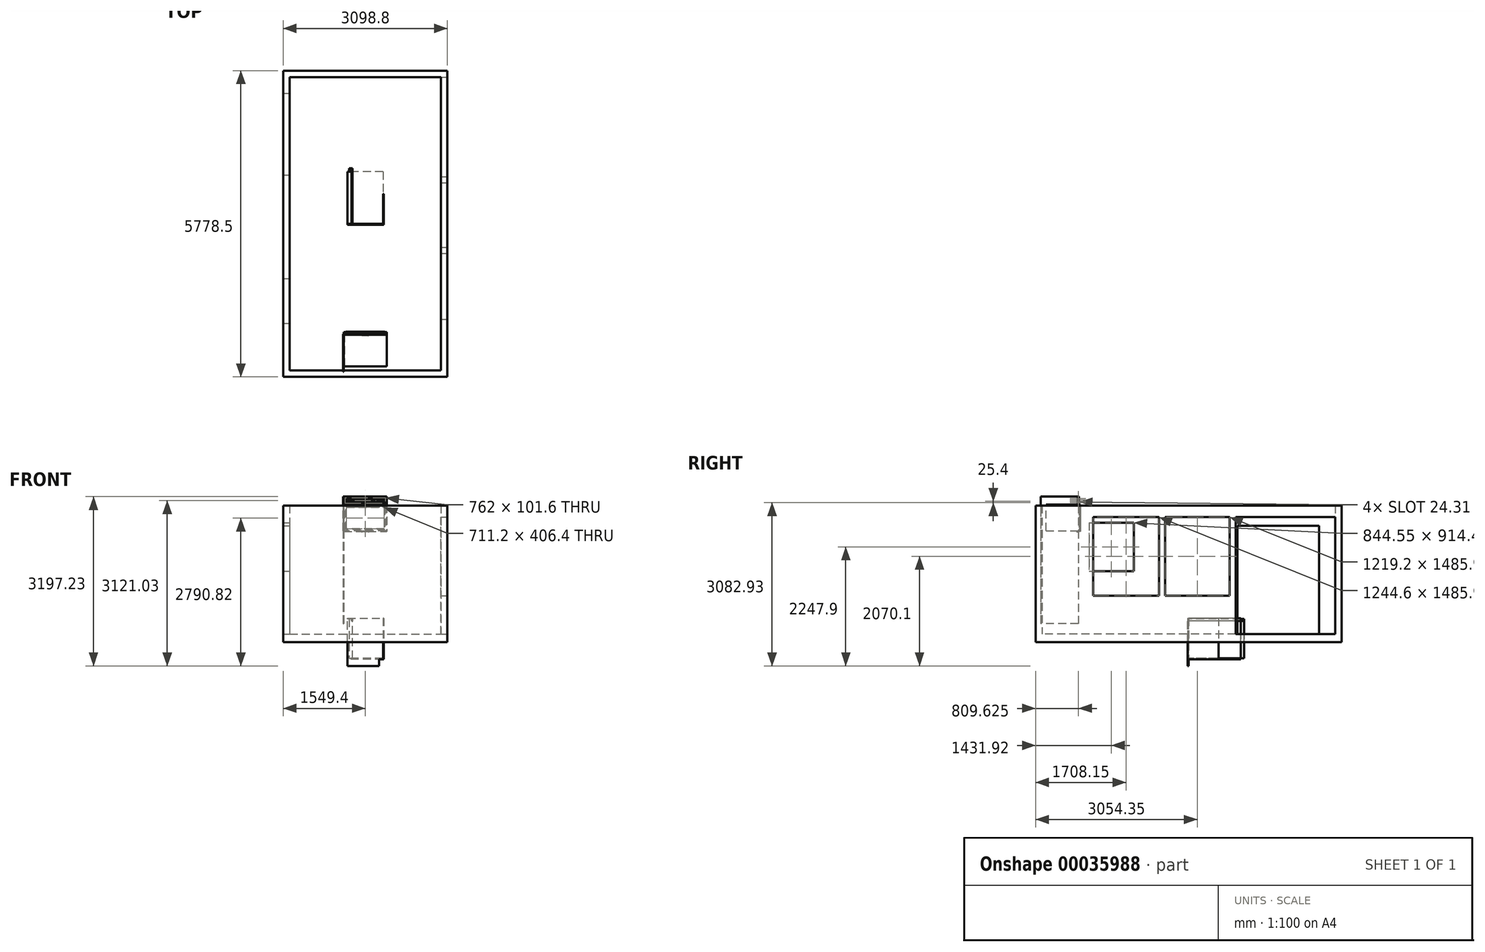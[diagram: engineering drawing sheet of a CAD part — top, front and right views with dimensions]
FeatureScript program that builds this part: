
annotation { "Feature Type Name" : "Feature", "Feature Type Description" : "" }
export const myFeature = defineFeature(function(context is Context, id is Id, definition is map)
    precondition{}
    {
        {
            var Q0;
            Q0=qCreatedBy(makeId("Top.planeOp"),FACE);
            var sketch = newSketch(context, id + "F0", { "sketchPlane" : qUnion([Q0])});
            skLineSegment(sketch, "E0.bottom", {"start": v(-1549.4, 2889.25) * mm, "end": v(1549.4, 2889.25) * mm});
            skLineSegment(sketch, "E0.top", {"start": v(-1549.4, -2889.25) * mm, "end": v(1549.4, -2889.25) * mm});
            skLineSegment(sketch, "E0.left", {"start": v(-1549.4, 2889.25) * mm, "end": v(-1549.4, -2889.25) * mm});
            skLineSegment(sketch, "E0.right", {"start": v(1549.4, 2889.25) * mm, "end": v(1549.4, -2889.25) * mm});
            skLineSegment(sketch, "E1", {"start": v(1549.4, 2889.25) * mm, "end": v(-1549.4, -2889.25) * mm, "construction": true});
            skSolve(sketch);
        }
        {
            var Q0;
            Q0 = qSketchRegion(id + "F0", true);
            extrude(context, id + "F1", {"entities" : qUnion([Q0]), "depth" : 152.4 * mm});
        }
        {
            var Q0;
            Q0=makeQuery(id+"F1.opExtrude","CAP_FACE",FACE,{"disambiguationData":[OSD([sQuery(id+"F0.wireOp",EDGE,"E0.bottom"),sQuery(id+"F0.wireOp",EDGE,"E0.top"),sQuery(id+"F0.wireOp",EDGE,"E0.left"),sQuery(id+"F0.wireOp",EDGE,"E0.right")])],"isStart":false});
            var sketch = newSketch(context, id + "F2", { "sketchPlane" : qUnion([Q0])});
            skLineSegment(sketch, "E2.0", {"start": v(-1549.4, 2889.25) * mm, "end": v(-1549.4, -2889.25) * mm});
            skLineSegment(sketch, "E3.0", {"start": v(-1549.4, -2889.25) * mm, "end": v(1549.4, -2889.25) * mm});
            skLineSegment(sketch, "E4.0", {"start": v(1549.4, 2889.25) * mm, "end": v(1549.4, -2889.25) * mm});
            skLineSegment(sketch, "E5.0", {"start": v(-1549.4, 2889.25) * mm, "end": v(1549.4, 2889.25) * mm});
            skLineSegment(sketch, "E6.0", {"start": v(-1428.75, 2768.6) * mm, "end": v(-1428.75, -2768.6) * mm});
            skLineSegment(sketch, "E6.1", {"start": v(-1428.75, 2768.6) * mm, "end": v(1428.75, 2768.6) * mm});
            skLineSegment(sketch, "E6.2", {"start": v(1428.75, 2768.6) * mm, "end": v(1428.75, -2768.6) * mm});
            skLineSegment(sketch, "E6.3", {"start": v(-1428.75, -2768.6) * mm, "end": v(1428.75, -2768.6) * mm});
            skSolve(sketch);
        }
        {
            var Q0;
            Q0=makeQuery(id+"F2.imprint","IMPRINT",FACE,{"disambiguationData":[TD([[makeQuery(id+"F2.imprint","IMPRINT",EDGE,{"derivedFrom":sQuery(id+"F2.wireOp",EDGE,"E2.0")}),1.0]])]});
            extrude(context, id + "F3", {"entities" : qUnion([Q0]), "operationType" : NewBodyOperationType.ADD, "depth" : 2425.7 * mm});
        }
        {
            var Q0;
            Q0=makeQuery(id+"F3.boolean.opBoolean","MERGE",FACE,{"derivedFrom":[makeQuery(id+"F1.opExtrude","SWEPT_FACE",FACE,{"disambiguationData":[OSD([sQuery(id+"F0.wireOp",EDGE,"E0.right")])]}),makeQuery(id+"F3.opExtrude","SWEPT_FACE",FACE,{"disambiguationData":[OSD([sQuery(id+"F2.wireOp",EDGE,"E4.0")])]})]});
            var sketch = newSketch(context, id + "F4", { "sketchPlane" : qUnion([Q0])});
            skLineSegment(sketch, "E7.0", {"start": v(2768.6, 2578.1) * mm, "end": v(2768.6, 152.4) * mm, "construction": true});
            skLineSegment(sketch, "E8.0", {"start": v(2768.6, 152.4) * mm, "end": v(-2768.6, 152.4) * mm, "construction": true});
            skLineSegment(sketch, "E9.0", {"start": v(2768.6, 2362.2) * mm, "end": v(-2768.6, 2362.2) * mm, "construction": true});
            skLineSegment(sketch, "E10.bottom", {"start": v(889, 2362.2) * mm, "end": v(2768.6, 2362.2) * mm});
            skLineSegment(sketch, "E10.top", {"start": v(889, 152.4) * mm, "end": v(2768.6, 152.4) * mm});
            skLineSegment(sketch, "E10.left", {"start": v(889, 2362.2) * mm, "end": v(889, 152.4) * mm});
            skLineSegment(sketch, "E10.right", {"start": v(2768.6, 2362.2) * mm, "end": v(2768.6, 152.4) * mm});
            skSolve(sketch);
        }
        {
            var Q0;
            Q0=makeQuery(id+"F4.imprint","IMPRINT",FACE,{"disambiguationData":[TD([[makeQuery(id+"F4.imprint","IMPRINT",EDGE,{"derivedFrom":sQuery(id+"F4.wireOp",EDGE,"E10.bottom")}),-1.0]])]});
            var Q1;
            Q1=makeQuery(id+"F3.opExtrude","SWEPT_FACE",FACE,{"disambiguationData":[OSD([sQuery(id+"F2.wireOp",EDGE,"E6.2")])]});
            extrude(context, id + "F5", {"entities" : qUnion([Q0]), "operationType" : NewBodyOperationType.REMOVE, "endBound" : BoundingType.UP_TO_SURFACE, "oppositeDirection" : true, "endBoundEntityFace" : qUnion([Q1]), "depth" : 25.4 * mm});
        }
        {
            var Q0;
            Q0=makeQuery(id+"F3.boolean.opBoolean","MERGE",FACE,{"derivedFrom":[makeQuery(id+"F1.opExtrude","SWEPT_FACE",FACE,{"disambiguationData":[OSD([sQuery(id+"F0.wireOp",EDGE,"E0.right")])]}),makeQuery(id+"F3.opExtrude","SWEPT_FACE",FACE,{"disambiguationData":[OSD([sQuery(id+"F2.wireOp",EDGE,"E4.0")])]})]});
            var sketch = newSketch(context, id + "F6", { "sketchPlane" : qUnion([Q0])});
            skLineSegment(sketch, "E11.bottom", {"start": v(-1803.4, 2362.2) * mm, "end": v(-558.8, 2362.2) * mm});
            skLineSegment(sketch, "E11.top", {"start": v(-1803.4, 876.3) * mm, "end": v(-558.8, 876.3) * mm});
            skLineSegment(sketch, "E11.left", {"start": v(-1803.4, 2362.2) * mm, "end": v(-1803.4, 876.3) * mm});
            skLineSegment(sketch, "E11.right", {"start": v(-558.8, 2362.2) * mm, "end": v(-558.8, 876.3) * mm});
            skLineSegment(sketch, "E12.bottom", {"start": v(-444.5, 2362.2) * mm, "end": v(774.7, 2362.2) * mm});
            skLineSegment(sketch, "E12.top", {"start": v(-444.5, 876.3) * mm, "end": v(774.7, 876.3) * mm});
            skLineSegment(sketch, "E12.left", {"start": v(-444.5, 2362.2) * mm, "end": v(-444.5, 876.3) * mm});
            skLineSegment(sketch, "E12.right", {"start": v(774.7, 2362.2) * mm, "end": v(774.7, 876.3) * mm});
            skLineSegment(sketch, "E13.0", {"start": v(-2768.6, 2578.1) * mm, "end": v(-2768.6, 152.4) * mm, "construction": true});
            skSolve(sketch);
        }
        {
            var Q0;
            Q0=makeQuery(id+"F6.imprint","IMPRINT",FACE,{"disambiguationData":[TD([[makeQuery(id+"F6.imprint","IMPRINT",EDGE,{"derivedFrom":sQuery(id+"F6.wireOp",EDGE,"E12.bottom")}),-1.0]])]});
            var Q1;
            Q1=makeQuery(id+"F6.imprint","IMPRINT",FACE,{"disambiguationData":[TD([[makeQuery(id+"F6.imprint","IMPRINT",EDGE,{"derivedFrom":sQuery(id+"F6.wireOp",EDGE,"E11.bottom")}),-1.0]])]});
            var Q2;
            Q2=makeQuery(id+"F3.opExtrude","SWEPT_FACE",FACE,{"disambiguationData":[OSD([sQuery(id+"F2.wireOp",EDGE,"E6.2")])]});
            extrude(context, id + "F7", {"entities" : qUnion([Q0, Q1]), "operationType" : NewBodyOperationType.REMOVE, "endBound" : BoundingType.UP_TO_SURFACE, "oppositeDirection" : true, "endBoundEntityFace" : qUnion([Q2]), "depth" : 25.4 * mm});
        }
        {
            var Q0;
            Q0=makeQuery(id+"F3.opExtrude","SWEPT_FACE",FACE,{"disambiguationData":[OSD([sQuery(id+"F2.wireOp",EDGE,"E6.0")])]});
            var sketch = newSketch(context, id + "F8", { "sketchPlane" : qUnion([Q0])});
            skLineSegment(sketch, "E14.bottom", {"start": v(-1879.6, 2254.25) * mm, "end": v(-1035.05, 2254.25) * mm});
            skLineSegment(sketch, "E14.top", {"start": v(-1879.6, 1339.85) * mm, "end": v(-1035.05, 1339.85) * mm});
            skLineSegment(sketch, "E14.left", {"start": v(-1879.6, 2254.25) * mm, "end": v(-1879.6, 1339.85) * mm});
            skLineSegment(sketch, "E14.right", {"start": v(-1035.05, 2254.25) * mm, "end": v(-1035.05, 1339.85) * mm});
            skSolve(sketch);
        }
        {
            var Q0;
            Q0=makeQuery(id+"F8.imprint","IMPRINT",FACE,{"disambiguationData":[TD([[makeQuery(id+"F8.imprint","IMPRINT",EDGE,{"derivedFrom":sQuery(id+"F8.wireOp",EDGE,"E14.bottom")}),-1.0]])]});
            extrude(context, id + "F9", {"entities" : qUnion([Q0]), "operationType" : NewBodyOperationType.REMOVE, "endBound" : BoundingType.THROUGH_ALL, "oppositeDirection" : true, "depth" : 25.4 * mm});
        }
        {
            var Q0;
            Q0=makeQuery(id+"F3.opExtrude","SWEPT_FACE",FACE,{"disambiguationData":[OSD([sQuery(id+"F2.wireOp",EDGE,"E6.0")])]});
            var sketch = newSketch(context, id + "F10", { "sketchPlane" : qUnion([Q0])});
            skLineSegment(sketch, "E15.bottom", {"start": v(920.75, 2197.1) * mm, "end": v(2463.8, 2197.1) * mm});
            skLineSegment(sketch, "E15.top", {"start": v(920.75, 152.4) * mm, "end": v(2463.8, 152.4) * mm});
            skLineSegment(sketch, "E15.left", {"start": v(920.75, 2197.1) * mm, "end": v(920.75, 152.4) * mm});
            skLineSegment(sketch, "E15.right", {"start": v(2463.8, 2197.1) * mm, "end": v(2463.8, 152.4) * mm});
            skSolve(sketch);
        }
        {
            var Q0;
            Q0=makeQuery(id+"F10.imprint","IMPRINT",FACE,{"disambiguationData":[TD([[makeQuery(id+"F10.imprint","IMPRINT",EDGE,{"derivedFrom":sQuery(id+"F10.wireOp",EDGE,"E15.bottom")}),-1.0]])]});
            extrude(context, id + "F11", {"entities" : qUnion([Q0]), "operationType" : NewBodyOperationType.REMOVE, "endBound" : BoundingType.THROUGH_ALL, "oppositeDirection" : true, "depth" : 25.4 * mm});
        }
        {
            var Q0;
            Q0=makeQuery(id+"F11.boolean.opBoolean","MERGE",FACE,{"derivedFrom":[makeQuery(id+"F5.boolean.opBoolean","MERGE",FACE,{"derivedFrom":[makeQuery(id+"F1.opExtrude","CAP_FACE",FACE,{"disambiguationData":[OSD([sQuery(id+"F0.wireOp",EDGE,"E0.bottom"),sQuery(id+"F0.wireOp",EDGE,"E0.top"),sQuery(id+"F0.wireOp",EDGE,"E0.left"),sQuery(id+"F0.wireOp",EDGE,"E0.right")])],"isStart":false}),makeQuery(id+"F5.opExtrude","SWEPT_FACE",FACE,{"disambiguationData":[OSD([sQuery(id+"F4.wireOp",EDGE,"E10.top")])]})]}),makeQuery(id+"F11.opExtrude","SWEPT_FACE",FACE,{"disambiguationData":[OSD([sQuery(id+"F10.wireOp",EDGE,"E15.top")])]})]});
            var sketch = newSketch(context, id + "F12", { "sketchPlane" : qUnion([Q0])});
            skLineSegment(sketch, "E16.bottom", {"start": v(-495.3, -2057.4) * mm, "end": v(-406.4, -2057.4) * mm});
            skLineSegment(sketch, "E16.top", {"start": v(-495.3, -2768.6) * mm, "end": v(-406.4, -2768.6) * mm});
            skLineSegment(sketch, "E16.left", {"start": v(-495.3, -2057.4) * mm, "end": v(-495.3, -2768.6) * mm});
            skLineSegment(sketch, "E16.right", {"start": v(-406.4, -2057.4) * mm, "end": v(-406.4, -2768.6) * mm});
            skLineSegment(sketch, "E17", {"start": v(0, 0) * mm, "end": v(0, -2768.6) * mm, "construction": true});
            skLineSegment(sketch, "E18.MirrorCS", {"start": v(495.3, -2057.4) * mm, "end": v(495.3, -2768.6) * mm});
            skLineSegment(sketch, "E19.MirrorCS", {"start": v(495.3, -2768.6) * mm, "end": v(406.4, -2768.6) * mm});
            skLineSegment(sketch, "E20.MirrorCS", {"start": v(406.4, -2057.4) * mm, "end": v(406.4, -2768.6) * mm});
            skLineSegment(sketch, "E21.MirrorCS", {"start": v(495.3, -2057.4) * mm, "end": v(406.4, -2057.4) * mm});
            skSolve(sketch);
        }
        {
            var Q0;
            Q0=makeQuery(id+"Fm9rjHwg65ug6vY_1.boolean.opBoolean","MERGE",FACE,{"derivedFrom":[makeQuery(id+"F3.opExtrude","CAP_FACE",FACE,{"disambiguationData":[OSD([sQuery(id+"F2.wireOp",EDGE,"E2.0"),sQuery(id+"F2.wireOp",EDGE,"E3.0"),sQuery(id+"F2.wireOp",EDGE,"E4.0"),sQuery(id+"F2.wireOp",EDGE,"E5.0"),sQuery(id+"F2.wireOp",EDGE,"E6.0"),sQuery(id+"F2.wireOp",EDGE,"E6.1"),sQuery(id+"F2.wireOp",EDGE,"E6.2"),sQuery(id+"F2.wireOp",EDGE,"E6.3")])],"isStart":false}),makeQuery(id+"Fm9rjHwg65ug6vY_1.opExtrude","CAP_FACE",FACE,{"disambiguationData":[OSD([sQuery(id+"F12.wireOp",EDGE,"E16.bottom"),sQuery(id+"F12.wireOp",EDGE,"E16.top"),sQuery(id+"F12.wireOp",EDGE,"E16.left"),sQuery(id+"F12.wireOp",EDGE,"E16.right")])],"isStart":false}),makeQuery(id+"Fm9rjHwg65ug6vY_1.opExtrude","CAP_FACE",FACE,{"disambiguationData":[OSD([sQuery(id+"F12.wireOp",EDGE,"E18.MirrorCS"),sQuery(id+"F12.wireOp",EDGE,"E19.MirrorCS"),sQuery(id+"F12.wireOp",EDGE,"E20.MirrorCS"),sQuery(id+"F12.wireOp",EDGE,"E21.MirrorCS")])],"isStart":false})]});
            var sketch = newSketch(context, id + "F13", { "sketchPlane" : qUnion([Q0])});
            skLineSegment(sketch, "E22.bottom", {"start": v(-406.4, -2692.4) * mm, "end": v(406.4, -2692.4) * mm});
            skLineSegment(sketch, "E22.top", {"start": v(-406.4, -2082.8) * mm, "end": v(406.4, -2082.8) * mm});
            skLineSegment(sketch, "E22.left", {"start": v(-406.4, -2692.4) * mm, "end": v(-406.4, -2082.8) * mm});
            skLineSegment(sketch, "E22.right", {"start": v(406.4, -2692.4) * mm, "end": v(406.4, -2082.8) * mm});
            skSolve(sketch);
        }
        {
            var Q0;
            Q0=makeQuery(id+"F13.imprint","IMPRINT",FACE,{"disambiguationData":[TD([[makeQuery(id+"F13.imprint","IMPRINT",EDGE,{"derivedFrom":sQuery(id+"F13.wireOp",EDGE,"E22.bottom")}),1.0]])]});
            extrude(context, id + "F14", {"entities" : qUnion([Q0]), "depth" : 15.88 * mm});
        }
        {
            var Q0;
            Q0=makeQuery(id+"F14.opExtrude","SWEPT_FACE",FACE,{"disambiguationData":[OSD([sQuery(id+"F13.wireOp",EDGE,"E22.top")])]});
            var sketch = newSketch(context, id + "F15", { "sketchPlane" : qUnion([Q0])});
            skLineSegment(sketch, "E23.bottom", {"start": v(390.53, 2578.1) * mm, "end": v(406.4, 2578.1) * mm});
            skLineSegment(sketch, "E23.top", {"start": v(390.53, 2101.85) * mm, "end": v(406.4, 2101.85) * mm});
            skLineSegment(sketch, "E23.left", {"start": v(390.53, 2578.1) * mm, "end": v(390.53, 2101.85) * mm});
            skLineSegment(sketch, "E23.right", {"start": v(406.4, 2578.1) * mm, "end": v(406.4, 2101.85) * mm});
            skLineSegment(sketch, "E24.bottom", {"start": v(-390.53, 2578.1) * mm, "end": v(390.53, 2578.1) * mm});
            skLineSegment(sketch, "E24.top", {"start": v(-390.53, 2101.85) * mm, "end": v(390.53, 2101.85) * mm});
            skLineSegment(sketch, "E24.left", {"start": v(-390.53, 2578.1) * mm, "end": v(-390.53, 2101.85) * mm});
            skSolve(sketch);
        }
        {
            var Q0;
            Q0=makeQuery(id+"F15.imprint","IMPRINT",FACE,{"disambiguationData":[TD([[makeQuery(id+"F15.imprint","IMPRINT",EDGE,{"derivedFrom":sQuery(id+"F15.wireOp",EDGE,"E24.bottom")}),1.0]])]});
            extrude(context, id + "F16", {"entities" : qUnion([Q0]), "depth" : 15.88 * mm});
        }
        {
            var Q0;
            Q0=makeQuery(id+"F15.imprint","IMPRINT",FACE,{"disambiguationData":[TD([[makeQuery(id+"F15.imprint","IMPRINT",EDGE,{"derivedFrom":sQuery(id+"F15.wireOp",EDGE,"E23.bottom")}),1.0]])]});
            var Q1;
            Q1=makeQuery(id+"F14.opExtrude","SWEPT_FACE",FACE,{"disambiguationData":[OSD([sQuery(id+"F13.wireOp",EDGE,"E22.bottom")])]});
            extrude(context, id + "F17", {"entities" : qUnion([Q0]), "endBound" : BoundingType.UP_TO_SURFACE, "oppositeDirection" : true, "endBoundEntityFace" : qUnion([Q1]), "depth" : 25.4 * mm});
        }
        {
            var Q0;
            Q0=makeQuery(id+"F15.imprint","IMPRINT",FACE,{"disambiguationData":[TD([[makeQuery(id+"F15.imprint","IMPRINT",EDGE,{"derivedFrom":sQuery(id+"F15.wireOp",EDGE,"E24.bottom")}),1.0]])]});
            extrude(context, id + "F18", {"entities" : qUnion([Q0]), "depth" : 15.88 * mm});
        }
        {
            var Q0;
            Q0=makeQuery(id+"F18.opExtrude","CAP_FACE",FACE,{"disambiguationData":[OSD([sQuery(id+"F15.wireOp",EDGE,"E24.bottom"),sQuery(id+"F15.wireOp",EDGE,"E24.top"),sQuery(id+"F15.wireOp",EDGE,"E24.left"),sQuery(id+"F15.wireOp",EDGE,"E23.left")])],"isStart":false});
            var sketch = newSketch(context, id + "F19", { "sketchPlane" : qUnion([Q0])});
            skLineSegment(sketch, "E25.rect.bottom", {"start": v(406.4, 2593.98) * mm, "end": v(-406.4, 2593.98) * mm});
            skLineSegment(sketch, "E25.rect.top", {"start": v(406.4, 2085.98) * mm, "end": v(-406.4, 2085.98) * mm});
            skLineSegment(sketch, "E25.rect.left", {"start": v(406.4, 2593.98) * mm, "end": v(406.4, 2085.98) * mm});
            skLineSegment(sketch, "E25.rect.right", {"start": v(-406.4, 2593.98) * mm, "end": v(-406.4, 2085.98) * mm});
            skPoint(sketch, "E25.rect.middle", {"position": v(0, 2339.98) * mm});
            skLineSegment(sketch, "E26.0", {"start": v(355.6, 2543.18) * mm, "end": v(-355.6, 2543.18) * mm});
            skLineSegment(sketch, "E26.1", {"start": v(355.6, 2543.18) * mm, "end": v(355.6, 2136.78) * mm});
            skLineSegment(sketch, "E26.2", {"start": v(355.6, 2136.78) * mm, "end": v(-355.6, 2136.78) * mm});
            skLineSegment(sketch, "E26.3", {"start": v(-355.6, 2543.18) * mm, "end": v(-355.6, 2136.78) * mm});
            skSolve(sketch);
        }
        {
            var Q0;
            Q0=makeQuery(id+"F19.imprint","IMPRINT",FACE,{"disambiguationData":[TD([[makeQuery(id+"F19.imprint","IMPRINT",EDGE,{"derivedFrom":sQuery(id+"F19.wireOp",EDGE,"E25.rect.bottom")}),1.0]])]});
            var Q1;
            Q1=makeQuery(id+"F19.imprint","IMPRINT",FACE,{"disambiguationData":[TD([[makeQuery(id+"F19.imprint","IMPRINT",EDGE,{"derivedFrom":sQuery(id+"F19.wireOp",EDGE,"E26.0")}),-1.0]])]});
            extrude(context, id + "F20", {"entities" : qUnion([Q0, Q1]), "depth" : 25.4 * mm});
        }
        {
            var Q0;
            Q0=makeQuery(id+"F20.opExtrude","SWEPT_FACE",FACE,{"disambiguationData":[OSD([sQuery(id+"F19.wireOp",EDGE,"E26.3")])]});
            var sketch = newSketch(context, id + "F21", { "sketchPlane" : qUnion([Q0])});
            skLineSegment(sketch, "E27.0", {"start": v(2041.53, 2136.78) * mm, "end": v(2066.93, 2136.78) * mm, "construction": true});
            skLineSegment(sketch, "E28.bottom", {"start": v(2046.3, 2136.78) * mm, "end": v(2041.53, 2136.78) * mm});
            skLineSegment(sketch, "E28.top", {"start": v(2046.3, 2124.08) * mm, "end": v(2041.53, 2124.08) * mm});
            skLineSegment(sketch, "E28.left", {"start": v(2046.3, 2136.78) * mm, "end": v(2046.3, 2124.08) * mm});
            skLineSegment(sketch, "E28.right", {"start": v(2041.53, 2136.78) * mm, "end": v(2041.53, 2124.08) * mm});
            skSolve(sketch);
        }
        {
            var Q0;
            Q0=makeQuery(id+"F20.opExtrude","CAP_FACE",FACE,{"disambiguationData":[OSD([sQuery(id+"F19.wireOp",EDGE,"E25.rect.bottom"),sQuery(id+"F19.wireOp",EDGE,"E25.rect.top"),sQuery(id+"F19.wireOp",EDGE,"E25.rect.left"),sQuery(id+"F19.wireOp",EDGE,"E25.rect.right"),sQuery(id+"F19.wireOp",EDGE,"E26.0"),sQuery(id+"F19.wireOp",EDGE,"E26.1"),sQuery(id+"F19.wireOp",EDGE,"E26.2"),sQuery(id+"F19.wireOp",EDGE,"E26.3")])],"isStart":false});
            var sketch = newSketch(context, id + "F22", { "sketchPlane" : qUnion([Q0])});
            skLineSegment(sketch, "E29.0", {"start": v(355.6, 2543.18) * mm, "end": v(-355.6, 2543.18) * mm});
            skLineSegment(sketch, "E30.0", {"start": v(355.6, 2543.18) * mm, "end": v(355.6, 2136.78) * mm});
            skLineSegment(sketch, "E31.0", {"start": v(355.6, 2136.78) * mm, "end": v(-355.6, 2136.78) * mm});
            skLineSegment(sketch, "E32.0", {"start": v(-355.6, 2543.18) * mm, "end": v(-355.6, 2136.78) * mm});
            skSolve(sketch);
        }
        {
            var Q0;
            Q0 = qSketchRegion(id + "F21", true);
            var Q1;
            Q1 = qBodyType(qCreatedBy(id + "F22" ,EDGE), BodyType.WIRE);
            sweep(context, id + "F23", {"operationType" : NewBodyOperationType.REMOVE, "profiles" : qUnion([Q0]), "path" : qUnion([Q1])});
        }
        {
            var Q0;
            Q0=makeQuery(id+"F20.opExtrude","CAP_FACE",FACE,{"disambiguationData":[OSD([sQuery(id+"F19.wireOp",EDGE,"E25.rect.bottom"),sQuery(id+"F19.wireOp",EDGE,"E25.rect.top"),sQuery(id+"F19.wireOp",EDGE,"E25.rect.left"),sQuery(id+"F19.wireOp",EDGE,"E25.rect.right"),sQuery(id+"F19.wireOp",EDGE,"E26.0"),sQuery(id+"F19.wireOp",EDGE,"E26.1"),sQuery(id+"F19.wireOp",EDGE,"E26.2"),sQuery(id+"F19.wireOp",EDGE,"E26.3")])],"isStart":false});
            var sketch = newSketch(context, id + "F24", { "sketchPlane" : qUnion([Q0])});
            skLineSegment(sketch, "E33.0", {"start": v(368.3, 2555.87) * mm, "end": v(-368.3, 2555.87) * mm});
            skLineSegment(sketch, "E34.0", {"start": v(368.3, 2124.08) * mm, "end": v(368.3, 2555.87) * mm});
            skLineSegment(sketch, "E35.0", {"start": v(-368.3, 2124.08) * mm, "end": v(368.3, 2124.08) * mm});
            skLineSegment(sketch, "E36.0", {"start": v(-368.3, 2555.87) * mm, "end": v(-368.3, 2124.08) * mm});
            skSolve(sketch);
        }
        {
            var Q0;
            Q0=makeQuery(id+"F24.imprint","IMPRINT",FACE,{"disambiguationData":[TD([[makeQuery(id+"F24.imprint","IMPRINT",EDGE,{"derivedFrom":sQuery(id+"F24.wireOp",EDGE,"E33.0")}),1.0]])]});
            extrude(context, id + "F25", {"entities" : qUnion([Q0]), "depth" : 4.78 * mm});
        }
        {
            var Q0;
            Q0=makeQuery(id+"F20.opExtrude","SWEPT_FACE",FACE,{"disambiguationData":[OSD([sQuery(id+"F19.wireOp",EDGE,"E25.rect.top")])]});
            var sketch = newSketch(context, id + "F26", { "sketchPlane" : qUnion([Q0])});
            skLineSegment(sketch, "E37", {"start": v(-63.5, 2066.93) * mm, "end": v(-63.5, 2092.33) * mm});
            skLineSegment(sketch, "E38", {"start": v(-50.8, 2105.03) * mm, "end": v(50.8, 2105.03) * mm});
            skLineSegment(sketch, "E39", {"start": v(63.5, 2092.33) * mm, "end": v(63.5, 2066.93) * mm});
            skPoint(sketch, "E40.visualSharp", {"position": v(-63.5, 2105.03) * mm});
            skArc(sketch, "E40.filletArc", {"start": v(-50.8, 2105.03) * mm, "mid": v(-59.78, 2101.3) * mm, "end": v(-63.5, 2092.33) * mm});
            skPoint(sketch, "E41.visualSharp", {"position": v(63.5, 2105.03) * mm});
            skArc(sketch, "E41.filletArc", {"start": v(63.5, 2092.33) * mm, "mid": v(59.78, 2101.3) * mm, "end": v(50.8, 2105.03) * mm});
            skLineSegment(sketch, "E42.0", {"start": v(-406.4, 2066.93) * mm, "end": v(406.4, 2066.93) * mm, "construction": true});
            skPoint(sketch, "E43", {"position": v(0, 2066.93) * mm});
            skPoint(sketch, "E44", {"position": v(0, 2105.03) * mm});
            skSolve(sketch);
        }
        {
            var Q0;
            Q0=makeQuery(id+"F20.opExtrude","CAP_FACE",FACE,{"disambiguationData":[OSD([sQuery(id+"F19.wireOp",EDGE,"E25.rect.bottom"),sQuery(id+"F19.wireOp",EDGE,"E25.rect.top"),sQuery(id+"F19.wireOp",EDGE,"E25.rect.left"),sQuery(id+"F19.wireOp",EDGE,"E25.rect.right"),sQuery(id+"F19.wireOp",EDGE,"E26.0"),sQuery(id+"F19.wireOp",EDGE,"E26.1"),sQuery(id+"F19.wireOp",EDGE,"E26.2"),sQuery(id+"F19.wireOp",EDGE,"E26.3")])],"isStart":true});
            var sketch = newSketch(context, id + "F27", { "sketchPlane" : qUnion([Q0])});
            skCircle(sketch, "E45", {"center": v(63.5, 2085.98) * mm, "radius": 6.35 * mm});
            skSolve(sketch);
        }
        {
            var Q0;
            {var subQ0=makeQuery(id+"F20.opExtrude","CAP_EDGE",EDGE,{"disambiguationData":[OSD([sQuery(id+"F19.wireOp",EDGE,"E25.rect.top")])],"isStart":true});var subQ1=sQuery(id+"F27.wireOp",EDGE,"E45");var subQ3=makeQuery(id+"F27.imprint","INTERSECT",VERTEX,{"disambiguationData":[OD(0.0)],"derivedFrom":[subQ0,subQ1]});Q0=makeQuery(id+"F27.imprint","IMPRINT",FACE,{"disambiguationData":[TD([[makeQuery(id+"F27.imprint","IMPRINT",EDGE,{"disambiguationData":[TD([[subQ3,-1.0]])],"derivedFrom":subQ1}),1.0]])]});}
            var Q1;
            {var subQ0=makeQuery(id+"F20.opExtrude","CAP_EDGE",EDGE,{"disambiguationData":[OSD([sQuery(id+"F19.wireOp",EDGE,"E25.rect.top")])],"isStart":true});var subQ1=sQuery(id+"F27.wireOp",EDGE,"E45");var subQ3=makeQuery(id+"F27.imprint","INTERSECT",VERTEX,{"disambiguationData":[OD(0.0)],"derivedFrom":[subQ0,subQ1]});Q1=makeQuery(id+"F27.imprint","IMPRINT",FACE,{"disambiguationData":[TD([[makeQuery(id+"F27.imprint","IMPRINT",EDGE,{"disambiguationData":[TD([[subQ3,1.0]])],"derivedFrom":subQ1}),1.0]])]});}
            var Q2;
            Q2=sQuery(id+"F26.wireOp",EDGE,"E39");
            var Q3;
            Q3=sQuery(id+"F26.wireOp",EDGE,"E41.filletArc");
            var Q4;
            Q4=sQuery(id+"F26.wireOp",EDGE,"E38");
            var Q5;
            Q5=sQuery(id+"F26.wireOp",EDGE,"E40.filletArc");
            var Q6;
            Q6=sQuery(id+"F26.wireOp",EDGE,"E37");
            sweep(context, id + "F28", {"profiles" : qUnion([Q0, Q1]), "path" : qUnion([Q2, Q3, Q4, Q5, Q6])});
        }
        {
            var Q0;
            Q0=makeQuery(id+"F27.imprint","IMPRINT",FACE,{"disambiguationData":[TD([[makeQuery(id+"F27.imprint","IMPRINT",EDGE,{"derivedFrom":makeQuery(id+"F20.opExtrude","CAP_EDGE",EDGE,{"disambiguationData":[OSD([sQuery(id+"F19.wireOp",EDGE,"E25.rect.bottom")])],"isStart":true})}),-1.0]])]});
            var sketch = newSketch(context, id + "F29", { "sketchPlane" : qUnion([Q0])});
            skLineSegment(sketch, "E46.bottom", {"start": v(-406.4, 2746.38) * mm, "end": v(406.4, 2746.38) * mm});
            skLineSegment(sketch, "E46.top", {"start": v(-406.4, 2593.98) * mm, "end": v(406.4, 2593.98) * mm});
            skLineSegment(sketch, "E46.left", {"start": v(-406.4, 2746.38) * mm, "end": v(-406.4, 2593.98) * mm});
            skLineSegment(sketch, "E46.right", {"start": v(406.4, 2746.38) * mm, "end": v(406.4, 2593.98) * mm});
            skLineSegment(sketch, "E47.0", {"start": v(-381, 2720.98) * mm, "end": v(381, 2720.98) * mm});
            skLineSegment(sketch, "E47.1", {"start": v(-381, 2720.98) * mm, "end": v(-381, 2619.38) * mm});
            skLineSegment(sketch, "E47.2", {"start": v(-381, 2619.38) * mm, "end": v(381, 2619.38) * mm});
            skLineSegment(sketch, "E47.3", {"start": v(381, 2720.98) * mm, "end": v(381, 2619.38) * mm});
            skSolve(sketch);
        }
        {
            var Q0;
            Q0=makeQuery(id+"F29.imprint","IMPRINT",FACE,{"disambiguationData":[TD([[makeQuery(id+"F29.imprint","IMPRINT",EDGE,{"derivedFrom":sQuery(id+"F29.wireOp",EDGE,"E46.bottom")}),-1.0]])]});
            extrude(context, id + "F30", {"entities" : qUnion([Q0]), "depth" : 25.4 * mm});
        }
        {
            var Q0;
            Q0=makeQuery(id+"F30.opExtrude","SWEPT_FACE",FACE,{"disambiguationData":[OSD([sQuery(id+"F29.wireOp",EDGE,"E46.left")])]});
            var sketch = newSketch(context, id + "F31", { "sketchPlane" : qUnion([Q0])});
            skLineSegment(sketch, "E48.0", {"start": v(2092.33, 2619.38) * mm, "end": v(2066.93, 2619.38) * mm, "construction": true});
            skLineSegment(sketch, "E49.0", {"start": v(2092.33, 2720.98) * mm, "end": v(2066.93, 2720.98) * mm, "construction": true});
            skLineSegment(sketch, "E50", {"start": v(2079.62, 2720.98) * mm, "end": v(2079.62, 2619.38) * mm, "construction": true});
            skLineSegment(sketch, "E51", {"start": v(2072.89, 2643.3) * mm, "end": v(2090.85, 2625.34) * mm});
            skLineSegment(sketch, "E52", {"start": v(2086.36, 2620.85) * mm, "end": v(2068.4, 2638.81) * mm});
            skArc(sketch, "E53", {"start": v(2072.89, 2643.3) * mm, "mid": v(2068.4, 2643.3) * mm, "end": v(2068.4, 2638.81) * mm});
            skPoint(sketch, "E53.first.point", {"position": v(2068.4, 2638.81) * mm});
            skPoint(sketch, "E53.second.point", {"position": v(2072.89, 2643.3) * mm});
            skArc(sketch, "E54", {"start": v(2086.36, 2620.85) * mm, "mid": v(2090.85, 2620.85) * mm, "end": v(2090.85, 2625.34) * mm});
            skPoint(sketch, "E54.first.point", {"position": v(2086.36, 2620.85) * mm});
            skPoint(sketch, "E54.second.point", {"position": v(2090.85, 2625.34) * mm});
            skLineSegment(sketch, "E55", {"start": v(2070.64, 2641.06) * mm, "end": v(2088.6, 2623.1) * mm, "construction": true});
            skPoint(sketch, "E56", {"position": v(2079.62, 2632.08) * mm});
            skLineSegment(sketch, "E57.0.1.0", {"start": v(2086.36, 2646.25) * mm, "end": v(2068.4, 2664.21) * mm});
            skLineSegment(sketch, "E57.0.1.1", {"start": v(2072.89, 2668.7) * mm, "end": v(2090.85, 2650.74) * mm});
            skArc(sketch, "E57.0.1.2", {"start": v(2086.36, 2646.25) * mm, "mid": v(2090.85, 2646.25) * mm, "end": v(2090.85, 2650.74) * mm});
            skArc(sketch, "E57.0.1.3", {"start": v(2072.89, 2668.7) * mm, "mid": v(2068.4, 2668.7) * mm, "end": v(2068.4, 2664.21) * mm});
            skLineSegment(sketch, "E57.0.2.0", {"start": v(2086.36, 2671.65) * mm, "end": v(2068.4, 2689.61) * mm});
            skLineSegment(sketch, "E57.0.2.1", {"start": v(2072.89, 2694.1) * mm, "end": v(2090.85, 2676.14) * mm});
            skArc(sketch, "E57.0.2.2", {"start": v(2086.36, 2671.65) * mm, "mid": v(2090.85, 2671.65) * mm, "end": v(2090.85, 2676.14) * mm});
            skArc(sketch, "E57.0.2.3", {"start": v(2072.89, 2694.1) * mm, "mid": v(2068.4, 2694.1) * mm, "end": v(2068.4, 2689.61) * mm});
            skLineSegment(sketch, "E57.0.3.0", {"start": v(2086.36, 2697.05) * mm, "end": v(2068.4, 2715.01) * mm});
            skLineSegment(sketch, "E57.0.3.1", {"start": v(2072.89, 2719.5) * mm, "end": v(2090.85, 2701.54) * mm});
            skArc(sketch, "E57.0.3.2", {"start": v(2086.36, 2697.05) * mm, "mid": v(2090.85, 2697.05) * mm, "end": v(2090.85, 2701.54) * mm});
            skArc(sketch, "E57.0.3.3", {"start": v(2072.89, 2719.5) * mm, "mid": v(2068.4, 2719.5) * mm, "end": v(2068.4, 2715.01) * mm});
            skLineSegment(sketch, "E57.direction1", {"start": v(2068.4, 2638.81) * mm, "end": v(2118.4, 2638.81) * mm, "construction": true});
            skLineSegment(sketch, "E57.direction2", {"start": v(2068.4, 2638.81) * mm, "end": v(2068.4, 2664.21) * mm, "construction": true});
            skSolve(sketch);
        }
        {
            var Q0;
            Q0=makeQuery(id+"F31.imprint","IMPRINT",FACE,{"disambiguationData":[TD([[makeQuery(id+"F31.imprint","IMPRINT",EDGE,{"derivedFrom":sQuery(id+"F31.wireOp",EDGE,"E57.0.3.0")}),-1.0]])]});
            var Q1;
            Q1=makeQuery(id+"F31.imprint","IMPRINT",FACE,{"disambiguationData":[TD([[makeQuery(id+"F31.imprint","IMPRINT",EDGE,{"derivedFrom":sQuery(id+"F31.wireOp",EDGE,"E57.0.2.0")}),-1.0]])]});
            var Q2;
            Q2=makeQuery(id+"F31.imprint","IMPRINT",FACE,{"disambiguationData":[TD([[makeQuery(id+"F31.imprint","IMPRINT",EDGE,{"derivedFrom":sQuery(id+"F31.wireOp",EDGE,"E57.0.1.0")}),-1.0]])]});
            var Q3;
            Q3=makeQuery(id+"F31.imprint","IMPRINT",FACE,{"disambiguationData":[TD([[makeQuery(id+"F31.imprint","IMPRINT",EDGE,{"derivedFrom":sQuery(id+"F31.wireOp",EDGE,"E51")}),-1.0]])]});
            var Q4;
            Q4=makeQuery(id+"F30.opExtrude","SWEPT_FACE",FACE,{"disambiguationData":[OSD([sQuery(id+"F29.wireOp",EDGE,"E47.3")])]});
            extrude(context, id + "F32", {"entities" : qUnion([Q0, Q1, Q2, Q3]), "operationType" : NewBodyOperationType.ADD, "endBound" : BoundingType.UP_TO_SURFACE, "oppositeDirection" : true, "endBoundEntityFace" : qUnion([Q4]), "depth" : 25.4 * mm});
        }
        {
            var Q0;
            Q0=qCreatedBy(makeId("Front.planeOp"),FACE);
            var sketch = newSketch(context, id + "F33", { "sketchPlane" : qUnion([Q0])});
            skLineSegment(sketch, "E58", {"start": v(-335.12, 450.85) * mm, "end": v(335.12, 450.85) * mm});
            skLineSegment(sketch, "E59", {"start": v(335.12, 450.85) * mm, "end": v(335.12, -323.85) * mm});
            skLineSegment(sketch, "E60", {"start": v(335.12, -323.85) * mm, "end": v(258.92, -323.85) * mm});
            skLineSegment(sketch, "E61", {"start": v(258.92, -323.85) * mm, "end": v(258.92, -450.85) * mm});
            skLineSegment(sketch, "E62", {"start": v(258.92, -450.85) * mm, "end": v(-335.12, -450.85) * mm});
            skLineSegment(sketch, "E63", {"start": v(-335.12, -450.85) * mm, "end": v(-335.12, 450.85) * mm});
            skLineSegment(sketch, "E64", {"start": v(-335.12, -450.85) * mm, "end": v(335.12, 450.85) * mm, "construction": true});
            skSolve(sketch);
        }
        {
            var Q0;
            Q0=makeQuery(id+"F33.imprint","IMPRINT",FACE,{"disambiguationData":[TD([[makeQuery(id+"F33.imprint","IMPRINT",EDGE,{"derivedFrom":sQuery(id+"F33.wireOp",EDGE,"E58")}),-1.0]])]});
            extrude(context, id + "F34", {"entities" : qUnion([Q0]), "depth" : 15.88 * mm});
        }
        {
            var Q0;
            Q0=makeQuery(id+"F34.opExtrude","CAP_FACE",FACE,{"disambiguationData":[OSD([sQuery(id+"F33.wireOp",EDGE,"E58"),sQuery(id+"F33.wireOp",EDGE,"E59"),sQuery(id+"F33.wireOp",EDGE,"E60"),sQuery(id+"F33.wireOp",EDGE,"E61"),sQuery(id+"F33.wireOp",EDGE,"E62"),sQuery(id+"F33.wireOp",EDGE,"E63")])],"isStart":true});
            var sketch = newSketch(context, id + "F35", { "sketchPlane" : qUnion([Q0])});
            skLineSegment(sketch, "E65.bottom", {"start": v(258.92, 434.98) * mm, "end": v(335.12, 434.98) * mm});
            skLineSegment(sketch, "E65.top", {"start": v(258.92, 450.85) * mm, "end": v(335.12, 450.85) * mm});
            skLineSegment(sketch, "E65.left", {"start": v(258.92, 434.98) * mm, "end": v(258.92, 450.85) * mm});
            skLineSegment(sketch, "E65.right", {"start": v(335.12, 434.98) * mm, "end": v(335.12, 450.85) * mm});
            skSolve(sketch);
        }
        {
            var Q0;
            Q0=makeQuery(id+"F35.imprint","IMPRINT",FACE,{"disambiguationData":[TD([[makeQuery(id+"F35.imprint","IMPRINT",EDGE,{"derivedFrom":sQuery(id+"F35.wireOp",EDGE,"E65.bottom")}),1.0]])]});
            extrude(context, id + "F36", {"entities" : qUnion([Q0]), "depth" : 984.25 * mm});
        }
        {
            var Q0;
            Q0=makeQuery(id+"F34.opExtrude","CAP_FACE",FACE,{"disambiguationData":[OSD([sQuery(id+"F33.wireOp",EDGE,"E58"),sQuery(id+"F33.wireOp",EDGE,"E59"),sQuery(id+"F33.wireOp",EDGE,"E60"),sQuery(id+"F33.wireOp",EDGE,"E61"),sQuery(id+"F33.wireOp",EDGE,"E62"),sQuery(id+"F33.wireOp",EDGE,"E63")])],"isStart":true});
            var sketch = newSketch(context, id + "F37", { "sketchPlane" : qUnion([Q0])});
            skLineSegment(sketch, "E66.bottom", {"start": v(-335.12, -307.98) * mm, "end": v(335.12, -307.98) * mm});
            skLineSegment(sketch, "E66.top", {"start": v(-335.12, -323.85) * mm, "end": v(335.12, -323.85) * mm});
            skLineSegment(sketch, "E66.left", {"start": v(-335.12, -307.98) * mm, "end": v(-335.12, -323.85) * mm});
            skLineSegment(sketch, "E66.right", {"start": v(335.12, -307.98) * mm, "end": v(335.12, -323.85) * mm});
            skSolve(sketch);
        }
        {
            var Q0;
            Q0=makeQuery(id+"F37.imprint","IMPRINT",FACE,{"disambiguationData":[TD([[makeQuery(id+"F37.imprint","IMPRINT",EDGE,{"derivedFrom":sQuery(id+"F37.wireOp",EDGE,"E66.bottom")}),-1.0]])]});
            extrude(context, id + "F38", {"entities" : qUnion([Q0]), "depth" : 984.25 * mm});
        }
        {
            var Q0;
            Q0=makeQuery(id+"F34.opExtrude","CAP_FACE",FACE,{"disambiguationData":[OSD([sQuery(id+"F33.wireOp",EDGE,"E58"),sQuery(id+"F33.wireOp",EDGE,"E59"),sQuery(id+"F33.wireOp",EDGE,"E60"),sQuery(id+"F33.wireOp",EDGE,"E61"),sQuery(id+"F33.wireOp",EDGE,"E62"),sQuery(id+"F33.wireOp",EDGE,"E63")])],"isStart":true});
            var sketch = newSketch(context, id + "F39", { "sketchPlane" : qUnion([Q0])});
            skLineSegment(sketch, "E67.bottom", {"start": v(243.05, 450.85) * mm, "end": v(258.92, 450.85) * mm});
            skLineSegment(sketch, "E67.top", {"start": v(243.05, 400.05) * mm, "end": v(258.92, 400.05) * mm});
            skLineSegment(sketch, "E67.left", {"start": v(243.05, 450.85) * mm, "end": v(243.05, 400.05) * mm});
            skLineSegment(sketch, "E67.right", {"start": v(258.92, 450.85) * mm, "end": v(258.92, 400.05) * mm});
            skSolve(sketch);
        }
        {
            var Q0;
            Q0=makeQuery(id+"F39.imprint","IMPRINT",FACE,{"disambiguationData":[TD([[makeQuery(id+"F39.imprint","IMPRINT",EDGE,{"derivedFrom":sQuery(id+"F39.wireOp",EDGE,"E67.bottom")}),1.0]])]});
            extrude(context, id + "F40", {"entities" : qUnion([Q0]), "depth" : 984.25 * mm});
        }
        {
            var Q0;
            Q0=makeQuery(id+"F36.opExtrude","CAP_FACE",FACE,{"disambiguationData":[OSD([sQuery(id+"F35.wireOp",EDGE,"E65.bottom"),sQuery(id+"F35.wireOp",EDGE,"E65.top"),sQuery(id+"F35.wireOp",EDGE,"E65.left"),sQuery(id+"F35.wireOp",EDGE,"E65.right")])],"isStart":false});
            var sketch = newSketch(context, id + "F41", { "sketchPlane" : qUnion([Q0])});
            skLineSegment(sketch, "E68", {"start": v(243.05, -307.98) * mm, "end": v(243.05, 400.05) * mm});
            skLineSegment(sketch, "E69", {"start": v(243.05, 400.05) * mm, "end": v(258.92, 400.05) * mm});
            skLineSegment(sketch, "E70", {"start": v(258.92, 400.05) * mm, "end": v(258.92, 434.98) * mm});
            skLineSegment(sketch, "E71", {"start": v(258.92, 434.98) * mm, "end": v(306.55, 434.98) * mm});
            skLineSegment(sketch, "E72", {"start": v(306.55, 434.98) * mm, "end": v(306.55, -307.98) * mm});
            skLineSegment(sketch, "E73", {"start": v(306.55, -307.98) * mm, "end": v(243.05, -307.98) * mm});
            skSolve(sketch);
        }
        {
            var Q0;
            Q0=makeQuery(id+"F41.imprint","IMPRINT",FACE,{"disambiguationData":[TD([[makeQuery(id+"F41.imprint","IMPRINT",EDGE,{"derivedFrom":sQuery(id+"F41.wireOp",EDGE,"E68")}),-1.0]])]});
            extrude(context, id + "F42", {"entities" : qUnion([Q0]), "depth" : 63.5 * mm});
        }
        {
            var Q0;
            Q0=makeQuery(id+"F38.opExtrude","SWEPT_FACE",FACE,{"disambiguationData":[OSD([sQuery(id+"F37.wireOp",EDGE,"E66.left")])]});
            var sketch = newSketch(context, id + "F43", { "sketchPlane" : qUnion([Q0])});
            skLineSegment(sketch, "E74.bottom", {"start": v(-15.88, 450.85) * mm, "end": v(565.15, 450.85) * mm});
            skLineSegment(sketch, "E74.top", {"start": v(-15.87, -323.85) * mm, "end": v(565.15, -323.85) * mm});
            skLineSegment(sketch, "E74.left", {"start": v(-15.88, 450.85) * mm, "end": v(-15.87, -323.85) * mm});
            skLineSegment(sketch, "E74.right", {"start": v(565.15, 450.85) * mm, "end": v(565.15, -323.85) * mm});
            skSolve(sketch);
        }
        {
            var Q0;
            {var subQ2=sQuery(id+"F43.wireOp",EDGE,"E74.bottom");Q0=makeQuery(id+"F43.imprint","IMPRINT",FACE,{"disambiguationData":[TD([[makeQuery(id+"F43.imprint","IMPRINT",EDGE,{"derivedFrom":subQ2}),-1.0]])]});}
            var Q1;
            {var subQ0=sQuery(id+"F37.wireOp",EDGE,"E66.left");var subQ4=makeQuery(id+"F38.opExtrude","CAP_EDGE",EDGE,{"disambiguationData":[OSD([subQ0])],"isStart":true});Q1=makeQuery(id+"F43.imprint","IMPRINT",FACE,{"disambiguationData":[TD([[makeQuery(id+"F43.imprint","IMPRINT",EDGE,{"derivedFrom":subQ4}),1.0]])]});}
            extrude(context, id + "F44", {"entities" : qUnion([Q0, Q1]), "depth" : 15.88 * mm});
        }
        {
            var Q0;
            Q0=makeQuery(id+"F17.opExtrude","SWEPT_FACE",FACE,{"disambiguationData":[OSD([sQuery(id+"F15.wireOp",EDGE,"E23.right")])]});
            var sketch = newSketch(context, id + "F45", { "sketchPlane" : qUnion([Q0])});
            skLineSegment(sketch, "E75.bottom", {"start": v(2082.8, 2746.38) * mm, "end": v(2794, 2746.38) * mm});
            skLineSegment(sketch, "E75.top", {"start": v(2082.8, 346.08) * mm, "end": v(2794, 346.08) * mm});
            skLineSegment(sketch, "E75.left", {"start": v(2082.8, 2746.38) * mm, "end": v(2082.8, 346.08) * mm});
            skLineSegment(sketch, "E75.right", {"start": v(2794, 2746.38) * mm, "end": v(2794, 346.08) * mm});
            skSolve(sketch);
        }
        {
            var Q0;
            {var subQ2=sQuery(id+"F45.wireOp",EDGE,"E75.bottom");Q0=makeQuery(id+"F45.imprint","IMPRINT",FACE,{"disambiguationData":[TD([[makeQuery(id+"F45.imprint","IMPRINT",EDGE,{"derivedFrom":subQ2}),-1.0]])]});}
            var Q1;
            {var subQ1=sQuery(id+"F15.wireOp",EDGE,"E23.right");Q1=makeQuery(id+"F45.imprint","IMPRINT",FACE,{"disambiguationData":[TD([[makeQuery(id+"F45.imprint","IMPRINT",EDGE,{"derivedFrom":makeQuery(id+"F17.opExtrude","TWEAK_EDGE",EDGE,{"derivedFrom":[makeQuery(id+"F14.opExtrude","SWEPT_FACE",FACE,{"disambiguationData":[OSD([sQuery(id+"F13.wireOp",EDGE,"E22.bottom")])]}),makeQuery(id+"F15.imprint","IMPRINT",EDGE,{"derivedFrom":subQ1})]})}),1.0]])]});}
            extrude(context, id + "F46", {"entities" : qUnion([Q0, Q1]), "depth" : 15.88 * mm});
        }
    });
